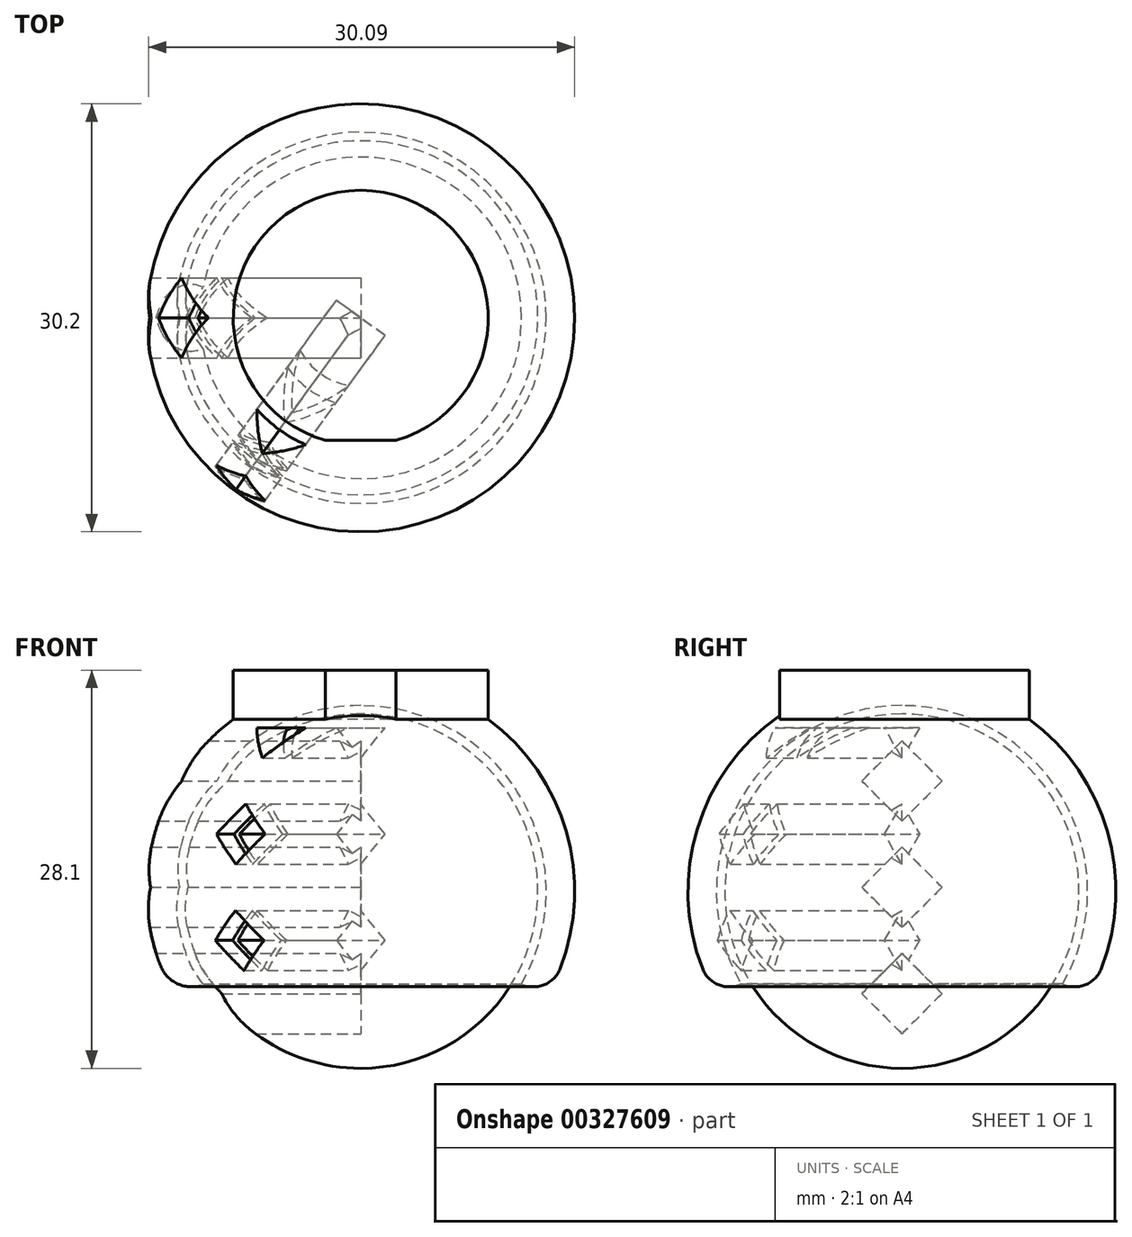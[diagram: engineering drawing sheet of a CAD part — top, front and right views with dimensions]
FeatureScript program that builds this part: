
annotation { "Feature Type Name" : "Feature", "Feature Type Description" : "" }
export const myFeature = defineFeature(function(context is Context, id is Id, definition is map)
    precondition{}
    {
        {
            var Q0;
            Q0=qCreatedBy(makeId("Front.planeOp"),FACE);
            var sketch = newSketch(context, id + "F0", { "sketchPlane" : qUnion([Q0])});
            skArc(sketch, "E0", {"start": v(0, 12.5) * mm, "mid": v(-12.5, 0) * mm, "end": v(0, -12.5) * mm});
            skLineSegment(sketch, "E1", {"start": v(0, 12.5) * mm, "end": v(0, -12.5) * mm});
            skSolve(sketch);
        }
        {
            var Q0;
            Q0=makeQuery(id+"F0.imprint","IMPRINT",FACE,{"disambiguationData":[TD([[makeQuery(id+"F0.imprint","IMPRINT",EDGE,{"derivedFrom":sQuery(id+"F0.wireOp",EDGE,"E0")}),1.0]])]});
            var Q1;
            Q1=sQuery(id+"F0.wireOp",EDGE,"E1");
            revolve(context, id + "F1", {"entities" : qUnion([Q0]), "axis" : qUnion([Q1]), "revolveType" : RevolveType.FULL});
        }
        {
            var Q0;
            Q0=qCreatedBy(makeId("Front.planeOp"),FACE);
            var sketch = newSketch(context, id + "F2", { "sketchPlane" : qUnion([Q0])});
            skArc(sketch, "E2.0", {"start": v(0, 13.1) * mm, "mid": v(-11.34, 6.55) * mm, "end": v(-11.34, -6.55) * mm});
            skArc(sketch, "E3.0", {"start": v(0, 15.1) * mm, "mid": v(-13.08, 7.55) * mm, "end": v(-13.08, -7.55) * mm});
            skLineSegment(sketch, "E4", {"start": v(0, 15.1) * mm, "end": v(0, 13.1) * mm});
            skLineSegment(sketch, "E5", {"start": v(0, 0) * mm, "end": v(-13.08, -7.55) * mm});
            skLineSegment(sketch, "E6", {"start": v(0, 15.1) * mm, "end": v(0, 15.6) * mm});
            skLineSegment(sketch, "E7", {"start": v(0, 15.6) * mm, "end": v(-9, 15.6) * mm});
            skLineSegment(sketch, "E8", {"start": v(-9, 15.6) * mm, "end": v(-9, 12.12) * mm});
            skSolve(sketch);
        }
        {
            var Q0;
            {var subQ0=sQuery(id+"F2.wireOp",EDGE,"E6");Q0=makeQuery(id+"F2.imprint","IMPRINT",FACE,{"disambiguationData":[TD([[makeQuery(id+"F2.imprint","IMPRINT",EDGE,{"derivedFrom":subQ0}),1.0]])]});}
            var Q1;
            {var subQ5=sQuery(id+"F2.wireOp",EDGE,"E2.0");Q1=makeQuery(id+"F2.imprint","IMPRINT",FACE,{"disambiguationData":[TD([[makeQuery(id+"F2.imprint","IMPRINT",EDGE,{"derivedFrom":subQ5}),-1.0]])]});}
            var Q2;
            Q2=sQuery(id+"F2.wireOp",EDGE,"E4");
            revolve(context, id + "F3", {"entities" : qUnion([Q0, Q1]), "axis" : qUnion([Q2]), "revolveType" : RevolveType.FULL});
        }
        {
            var Q0;
            Q0=makeQuery(id+"F3.opRevolve","SWEPT_FACE",FACE,{"disambiguationData":[OSD([sQuery(id+"F2.wireOp",EDGE,"E7")])]});
            var sketch = newSketch(context, id + "F4", { "sketchPlane" : qUnion([Q0])});
            skLineSegment(sketch, "E9.bottom", {"start": v(2.5, -8.65) * mm, "end": v(-2.5, -8.65) * mm});
            skLineSegment(sketch, "E9.top", {"start": v(2.5, -13.65) * mm, "end": v(-2.5, -13.65) * mm});
            skLineSegment(sketch, "E9.left", {"start": v(-2.5, -8.65) * mm, "end": v(-2.5, -13.65) * mm});
            skLineSegment(sketch, "E9.right", {"start": v(2.5, -8.65) * mm, "end": v(2.5, -13.65) * mm});
            skPoint(sketch, "E9.middle", {"position": v(0, -11.15) * mm});
            skSolve(sketch);
        }
        {
            var Q0;
            Q0 = qSketchRegion(id + "F4", true);
            var Q1;
            Q1=makeQuery(id+"F3.opRevolve","SWEPT_FACE",FACE,{"disambiguationData":[OSD([sQuery(id+"F2.wireOp",EDGE,"E3.0")])]});
            extrude(context, id + "F5", {"entities" : qUnion([Q0]), "operationType" : NewBodyOperationType.REMOVE, "endBound" : BoundingType.UP_TO_SURFACE, "oppositeDirection" : true, "endBoundEntityFace" : qUnion([Q1]), "depth" : 25 * mm});
        }
        {
            var Q0;
            Q0=makeQuery(id+"F3.opRevolve","SWEPT_EDGE",EDGE,{"disambiguationData":[OSD([sQuery(id+"F2.wireOp",EDGE,"E3.0"),sQuery(id+"F2.wireOp",EDGE,"E5")])]});
            fillet(context, id + "F6", {"entities" : qUnion([Q0]), "radius" : 2 * mm, "tangentPropagation" : true, "allowEdgeOverflow" : false});
        }
        {
            var Q0;
            Q0=qCreatedBy(makeId("Right.planeOp"),FACE);
            var sketch = newSketch(context, id + "F7", { "sketchPlane" : qUnion([Q0])});
            skLineSegment(sketch, "E10", {"start": v(0, -4.4) * mm, "end": v(2.83, -7.23) * mm});
            skLineSegment(sketch, "E11", {"start": v(2.83, -7.23) * mm, "end": v(0, -10.06) * mm});
            skLineSegment(sketch, "E12", {"start": v(0, -10.06) * mm, "end": v(-2.83, -7.23) * mm});
            skLineSegment(sketch, "E13", {"start": v(-2.83, -7.23) * mm, "end": v(0, -4.4) * mm});
            skLineSegment(sketch, "E14.1.0.0", {"start": v(-2.83, 0.27) * mm, "end": v(0, 3.1) * mm});
            skLineSegment(sketch, "E14.1.0.1", {"start": v(0, 3.1) * mm, "end": v(2.83, 0.27) * mm});
            skLineSegment(sketch, "E14.1.0.2", {"start": v(2.83, 0.27) * mm, "end": v(0, -2.56) * mm});
            skLineSegment(sketch, "E14.1.0.3", {"start": v(0, -2.56) * mm, "end": v(-2.83, 0.27) * mm});
            skLineSegment(sketch, "E14.2.0.0", {"start": v(-2.83, 7.77) * mm, "end": v(0, 10.6) * mm});
            skLineSegment(sketch, "E14.2.0.1", {"start": v(0, 10.6) * mm, "end": v(2.83, 7.77) * mm});
            skLineSegment(sketch, "E14.2.0.2", {"start": v(2.83, 7.77) * mm, "end": v(0, 4.94) * mm});
            skLineSegment(sketch, "E14.2.0.3", {"start": v(0, 4.94) * mm, "end": v(-2.83, 7.77) * mm});
            skLineSegment(sketch, "E14.direction1", {"start": v(-2.83, -7.23) * mm, "end": v(-2.83, 0.27) * mm, "construction": true});
            skSolve(sketch);
        }
        {
            var Q0;
            Q0 = qSketchRegion(id + "F7", true);
            extrude(context, id + "F8", {"entities" : qUnion([Q0]), "operationType" : NewBodyOperationType.REMOVE, "endBound" : BoundingType.THROUGH_ALL, "oppositeDirection" : true, "depth" : 25 * mm});
        }
        {
            var Q0;
            Q0=qCreatedBy(makeId("Front.planeOp"),FACE);
            var Q1;
            Q1=sQuery(id+"F0.wireOp",EDGE,"E1");
            cPlane(context, id + "F9", {"entities" : qUnion([Q0, Q1]), "cplaneType" : CPlaneType.LINE_ANGLE, "offset" : 25 * mm, "angle" : 36 * degree, "width" : 150 * mm, "height" : 150 * mm});
        }
        {
            var Q0;
            Q0=qCreatedBy(id+"F9.planeOp",FACE);
            var sketch = newSketch(context, id + "F10", { "sketchPlane" : qUnion([Q0])});
            skLineSegment(sketch, "E15", {"start": v(0, -1.36) * mm, "end": v(2.12, -3.48) * mm});
            skLineSegment(sketch, "E16", {"start": v(2.12, -3.48) * mm, "end": v(0, -5.6) * mm});
            skLineSegment(sketch, "E17", {"start": v(0, -5.6) * mm, "end": v(-2.12, -3.48) * mm});
            skLineSegment(sketch, "E18", {"start": v(-2.12, -3.48) * mm, "end": v(0, -1.36) * mm});
            skLineSegment(sketch, "E19.1.0.0", {"start": v(0, 6.14) * mm, "end": v(2.12, 4.02) * mm});
            skLineSegment(sketch, "E19.1.0.1", {"start": v(-2.12, 4.02) * mm, "end": v(0, 6.14) * mm});
            skLineSegment(sketch, "E19.1.0.2", {"start": v(0, 1.9) * mm, "end": v(-2.12, 4.02) * mm});
            skLineSegment(sketch, "E19.1.0.3", {"start": v(2.12, 4.02) * mm, "end": v(0, 1.9) * mm});
            skLineSegment(sketch, "E19.2.0.2", {"start": v(0, 9.4) * mm, "end": v(-2.12, 11.52) * mm});
            skLineSegment(sketch, "E19.2.0.3", {"start": v(2.12, 11.52) * mm, "end": v(0, 9.4) * mm});
            skLineSegment(sketch, "E19.direction1", {"start": v(2.12, -3.48) * mm, "end": v(2.12, 4.02) * mm, "construction": true});
            skLineSegment(sketch, "E20", {"start": v(2.12, 11.52) * mm, "end": v(-2.12, 11.52) * mm});
            skSolve(sketch);
        }
        {
            var Q0;
            Q0 = qSketchRegion(id + "F10", true);
            extrude(context, id + "F11", {"entities" : qUnion([Q0]), "operationType" : NewBodyOperationType.REMOVE, "oppositeDirection" : true, "depth" : 25 * mm});
        }
    });
